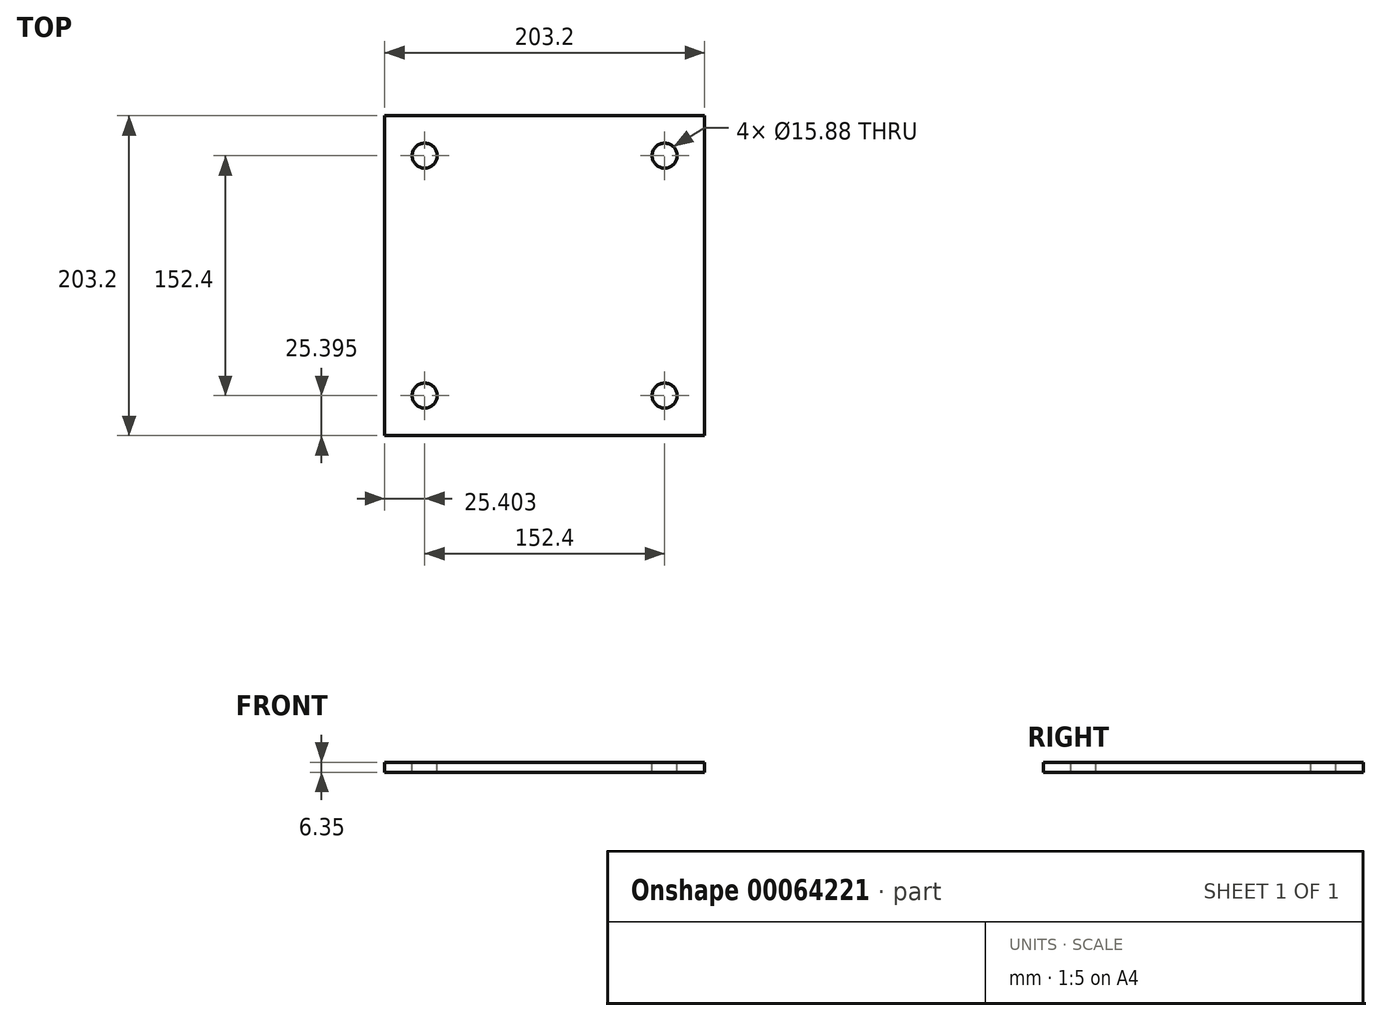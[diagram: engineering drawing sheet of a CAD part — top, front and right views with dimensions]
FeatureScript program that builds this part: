
annotation { "Feature Type Name" : "Feature", "Feature Type Description" : "" }
export const myFeature = defineFeature(function(context is Context, id is Id, definition is map)
    precondition{}
    {
        {
            var Q0;
            Q0=qCreatedBy(makeId("Top.planeOp"),FACE);
            var sketch = newSketch(context, id + "F0", { "sketchPlane" : qUnion([Q0])});
            skLineSegment(sketch, "E0.bottom", {"start": v(89.05, -206.65) * mm, "end": v(-114.15, -206.65) * mm});
            skLineSegment(sketch, "E0.top", {"start": v(89.05, -3.45) * mm, "end": v(-114.15, -3.45) * mm});
            skLineSegment(sketch, "E0.left", {"start": v(89.05, -206.65) * mm, "end": v(89.05, -3.45) * mm});
            skLineSegment(sketch, "E0.right", {"start": v(-114.15, -206.65) * mm, "end": v(-114.15, -3.45) * mm});
            skSolve(sketch);
        }
        {
            var Q0;
            Q0=makeQuery(id+"F0.imprint","IMPRINT",FACE,{"disambiguationData":[TD([[makeQuery(id+"F0.imprint","IMPRINT",EDGE,{"derivedFrom":sQuery(id+"F0.wireOp",EDGE,"E0.bottom")}),-1.0]])]});
            extrude(context, id + "F1", {"entities" : qUnion([Q0]), "depth" : 6.35 * mm});
        }
        {
            var Q0;
            Q0=makeQuery(id+"F1.opExtrude","CAP_FACE",FACE,{"disambiguationData":[OSD([sQuery(id+"F0.wireOp",EDGE,"E0.bottom"),sQuery(id+"F0.wireOp",EDGE,"E0.top"),sQuery(id+"F0.wireOp",EDGE,"E0.left"),sQuery(id+"F0.wireOp",EDGE,"E0.right")])],"isStart":false});
            var sketch = newSketch(context, id + "F2", { "sketchPlane" : qUnion([Q0])});
            skCircle(sketch, "E1", {"center": v(-88.75, -28.85) * mm, "radius": 7.94 * mm});
            skCircle(sketch, "E2", {"center": v(63.65, -28.85) * mm, "radius": 7.94 * mm});
            skCircle(sketch, "E3", {"center": v(-88.75, -181.25) * mm, "radius": 7.94 * mm});
            skCircle(sketch, "E4", {"center": v(63.65, -181.25) * mm, "radius": 7.94 * mm});
            skSolve(sketch);
        }
        {
            var Q0;
            Q0 = qSketchRegion(id + "F2", true);
            extrude(context, id + "F3", {"entities" : qUnion([Q0]), "operationType" : NewBodyOperationType.REMOVE, "oppositeDirection" : true, "depth" : 25.4 * mm});
        }
    });
